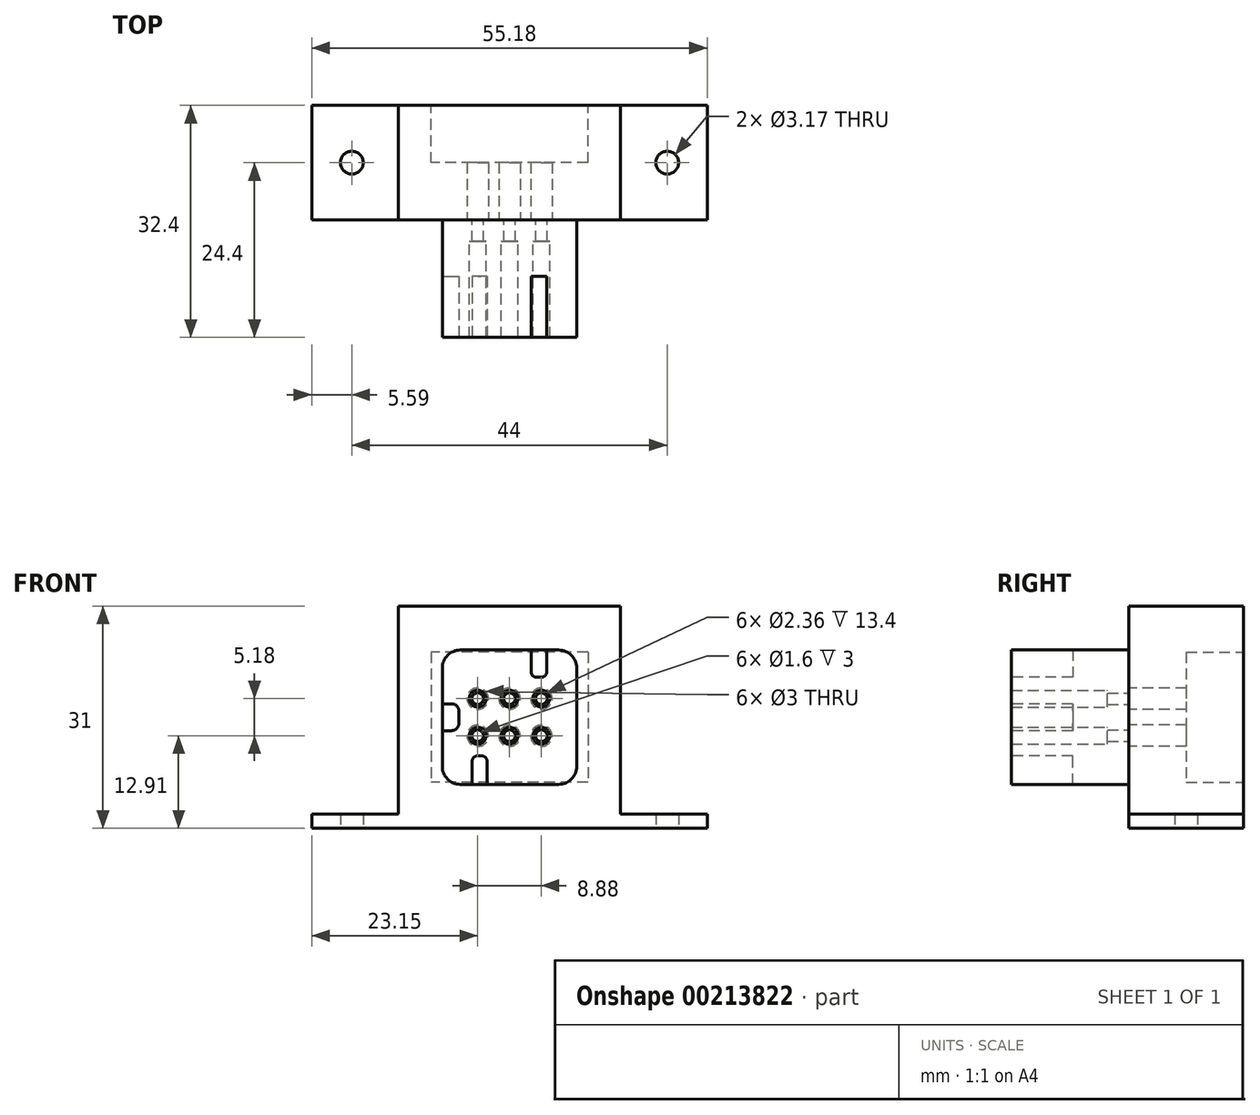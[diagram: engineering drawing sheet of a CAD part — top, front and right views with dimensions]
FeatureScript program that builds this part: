
annotation { "Feature Type Name" : "Feature", "Feature Type Description" : "" }
export const myFeature = defineFeature(function(context is Context, id is Id, definition is map)
    precondition{}
    {
        {
            var Q0;
            Q0=qCreatedBy(makeId("Front.planeOp"),FACE);
            var sketch = newSketch(context, id + "F0", { "sketchPlane" : qUnion([Q0])});
            skLineSegment(sketch, "E0.bottom", {"start": v(15.5, 15.5) * mm, "end": v(-15.5, 15.5) * mm});
            skLineSegment(sketch, "E0.top", {"start": v(15.5, -15.5) * mm, "end": v(-15.5, -15.5) * mm});
            skLineSegment(sketch, "E0.left", {"start": v(15.5, 15.5) * mm, "end": v(15.5, -15.5) * mm});
            skLineSegment(sketch, "E0.right", {"start": v(-15.5, 15.5) * mm, "end": v(-15.5, -15.5) * mm});
            skPoint(sketch, "E0.middle", {"position": v(0, 0) * mm});
            skCircle(sketch, "E1.0", {"center": v(-4.44, 2.6) * mm, "radius": 0.8 * mm, "construction": true});
            skCircle(sketch, "E2", {"center": v(-4.44, 2.6) * mm, "radius": 1.5 * mm});
            skCircle(sketch, "E3.1.0.0", {"center": v(0, 2.6) * mm, "radius": 1.5 * mm});
            skCircle(sketch, "E3.2.0.0", {"center": v(4.44, 2.6) * mm, "radius": 1.5 * mm});
            skLineSegment(sketch, "E3.direction1", {"start": v(-4.44, 2.6) * mm, "end": v(0, 2.6) * mm, "construction": true});
            skLineSegment(sketch, "E4", {"start": v(-15.5, 0) * mm, "end": v(15.5, 0) * mm, "construction": true});
            skCircle(sketch, "E5.MirrorC", {"center": v(-4.44, -2.6) * mm, "radius": 1.5 * mm});
            skCircle(sketch, "E6.MirrorC", {"center": v(0, -2.6) * mm, "radius": 1.5 * mm});
            skCircle(sketch, "E7.MirrorC", {"center": v(4.44, -2.6) * mm, "radius": 1.5 * mm});
            skLineSegment(sketch, "E8", {"start": v(0, 2.6) * mm, "end": v(0, -2.6) * mm, "construction": true});
            skSolve(sketch);
        }
        {
            var Q0;
            Q0 = qSketchRegion(id + "F0", true);
            extrude(context, id + "F1", {"entities" : qUnion([Q0]), "oppositeDirection" : true, "depth" : 16 * mm});
        }
        {
            var Q0;
            Q0=makeQuery(id+"F1.opExtrude","CAP_FACE",FACE,{"disambiguationData":[OSD([sQuery(id+"F0.wireOp",EDGE,"E0.bottom"),sQuery(id+"F0.wireOp",EDGE,"E0.top"),sQuery(id+"F0.wireOp",EDGE,"E0.left"),sQuery(id+"F0.wireOp",EDGE,"E0.right")])],"isStart":true});
            var sketch = newSketch(context, id + "F2", { "sketchPlane" : qUnion([Q0])});
            skLineSegment(sketch, "E9.bottom", {"start": v(6.87, 9.37) * mm, "end": v(-6.87, 9.37) * mm});
            skLineSegment(sketch, "E9.top", {"start": v(6.87, -9.37) * mm, "end": v(-6.87, -9.37) * mm});
            skLineSegment(sketch, "E9.left", {"start": v(9.37, 6.87) * mm, "end": v(9.37, -6.87) * mm});
            skLineSegment(sketch, "E9.right", {"start": v(-9.37, 6.87) * mm, "end": v(-9.37, -6.87) * mm});
            skPoint(sketch, "E9.middle", {"position": v(0, 0) * mm});
            skPoint(sketch, "E10.visualSharp", {"position": v(-9.37, 9.37) * mm});
            skArc(sketch, "E10.filletArc", {"start": v(-6.87, 9.37) * mm, "mid": v(-8.64, 8.64) * mm, "end": v(-9.37, 6.87) * mm});
            skPoint(sketch, "E11.visualSharp", {"position": v(9.37, 9.37) * mm});
            skArc(sketch, "E11.filletArc", {"start": v(9.37, 6.87) * mm, "mid": v(8.64, 8.64) * mm, "end": v(6.87, 9.37) * mm});
            skPoint(sketch, "E12.visualSharp", {"position": v(9.37, -9.37) * mm});
            skArc(sketch, "E12.filletArc", {"start": v(6.87, -9.37) * mm, "mid": v(8.64, -8.64) * mm, "end": v(9.37, -6.87) * mm});
            skPoint(sketch, "E13.visualSharp", {"position": v(-9.37, -9.37) * mm});
            skArc(sketch, "E13.filletArc", {"start": v(-9.37, -6.87) * mm, "mid": v(-8.64, -8.64) * mm, "end": v(-6.87, -9.37) * mm});
            skCircle(sketch, "E14", {"center": v(-4.44, 2.6) * mm, "radius": 1.18 * mm});
            skLineSegment(sketch, "E15", {"start": v(-9.37, 0) * mm, "end": v(9.37, 0) * mm, "construction": true});
            skCircle(sketch, "E16.1.0.0", {"center": v(0, 2.6) * mm, "radius": 1.18 * mm});
            skCircle(sketch, "E16.2.0.0", {"center": v(4.44, 2.6) * mm, "radius": 1.18 * mm});
            skLineSegment(sketch, "E16.direction1", {"start": v(-4.44, 2.6) * mm, "end": v(0, 2.6) * mm, "construction": true});
            skCircle(sketch, "E17.MirrorC", {"center": v(-4.44, -2.6) * mm, "radius": 1.18 * mm});
            skCircle(sketch, "E18.MirrorC", {"center": v(0, -2.6) * mm, "radius": 1.18 * mm});
            skCircle(sketch, "E19.MirrorC", {"center": v(4.44, -2.6) * mm, "radius": 1.18 * mm});
            skLineSegment(sketch, "E20.MirrorCS", {"start": v(-4.44, -2.6) * mm, "end": v(0, -2.6) * mm, "construction": true});
            skSolve(sketch);
        }
        {
            var Q0;
            Q0 = qSketchRegion(id + "F2", true);
            extrude(context, id + "F3", {"entities" : qUnion([Q0]), "depth" : 16.4 * mm});
        }
        {
            var Q0;
            Q0=makeQuery(id+"F3.opExtrude","CAP_FACE",FACE,{"disambiguationData":[OSD([sQuery(id+"F2.wireOp",EDGE,"E9.bottom"),sQuery(id+"F2.wireOp",EDGE,"E9.top"),sQuery(id+"F2.wireOp",EDGE,"E9.left"),sQuery(id+"F2.wireOp",EDGE,"E9.right"),sQuery(id+"F2.wireOp",EDGE,"E10.filletArc"),sQuery(id+"F2.wireOp",EDGE,"E11.filletArc"),sQuery(id+"F2.wireOp",EDGE,"E12.filletArc"),sQuery(id+"F2.wireOp",EDGE,"E13.filletArc"),sQuery(id+"F2.wireOp",EDGE,"E14"),sQuery(id+"F2.wireOp",EDGE,"E16.1.0.0"),sQuery(id+"F2.wireOp",EDGE,"E16.2.0.0"),sQuery(id+"F2.wireOp",EDGE,"E17.MirrorC"),sQuery(id+"F2.wireOp",EDGE,"E18.MirrorC"),sQuery(id+"F2.wireOp",EDGE,"E19.MirrorC")])],"isStart":false});
            var sketch = newSketch(context, id + "F4", { "sketchPlane" : qUnion([Q0])});
            skLineSegment(sketch, "E21.bottom", {"start": v(3, 9.37) * mm, "end": v(5.2, 9.37) * mm});
            skLineSegment(sketch, "E21.top", {"start": v(3.8, 5.57) * mm, "end": v(4.4, 5.57) * mm});
            skLineSegment(sketch, "E21.left", {"start": v(3, 9.37) * mm, "end": v(3, 6.37) * mm});
            skLineSegment(sketch, "E21.right", {"start": v(5.2, 9.37) * mm, "end": v(5.2, 6.37) * mm});
            skLineSegment(sketch, "E22.bottom", {"start": v(-5.22, -9.37) * mm, "end": v(-3.13, -9.37) * mm});
            skLineSegment(sketch, "E22.top", {"start": v(-4.42, -5.37) * mm, "end": v(-3.93, -5.37) * mm});
            skLineSegment(sketch, "E22.left", {"start": v(-5.22, -9.37) * mm, "end": v(-5.22, -6.17) * mm});
            skLineSegment(sketch, "E22.right", {"start": v(-3.13, -9.37) * mm, "end": v(-3.13, -6.17) * mm});
            skLineSegment(sketch, "E23.bottom", {"start": v(-9.37, 1.87) * mm, "end": v(-8.07, 1.87) * mm});
            skLineSegment(sketch, "E23.top", {"start": v(-9.37, -1.87) * mm, "end": v(-8.07, -1.87) * mm});
            skLineSegment(sketch, "E23.left", {"start": v(-9.37, 1.87) * mm, "end": v(-9.37, -1.87) * mm});
            skLineSegment(sketch, "E23.right", {"start": v(-7.07, 0.87) * mm, "end": v(-7.07, -0.87) * mm});
            skPoint(sketch, "E24.visualSharp", {"position": v(-7.07, 1.87) * mm});
            skArc(sketch, "E24.filletArc", {"start": v(-7.07, 0.87) * mm, "mid": v(-7.36, 1.58) * mm, "end": v(-8.07, 1.87) * mm});
            skPoint(sketch, "E25.visualSharp", {"position": v(-7.07, -1.87) * mm});
            skArc(sketch, "E25.filletArc", {"start": v(-8.07, -1.87) * mm, "mid": v(-7.36, -1.58) * mm, "end": v(-7.07, -0.87) * mm});
            skPoint(sketch, "E26.visualSharp", {"position": v(3, 5.57) * mm});
            skArc(sketch, "E26.filletArc", {"start": v(3, 6.37) * mm, "mid": v(3.24, 5.8) * mm, "end": v(3.8, 5.57) * mm});
            skPoint(sketch, "E27.visualSharp", {"position": v(5.2, 5.57) * mm});
            skArc(sketch, "E27.filletArc", {"start": v(4.4, 5.57) * mm, "mid": v(4.98, 5.8) * mm, "end": v(5.2, 6.37) * mm});
            skPoint(sketch, "E28.visualSharp", {"position": v(-5.22, -5.37) * mm});
            skArc(sketch, "E28.filletArc", {"start": v(-4.42, -5.37) * mm, "mid": v(-4.99, -5.6) * mm, "end": v(-5.22, -6.17) * mm});
            skPoint(sketch, "E29.visualSharp", {"position": v(-3.13, -5.37) * mm});
            skArc(sketch, "E29.filletArc", {"start": v(-3.13, -6.17) * mm, "mid": v(-3.36, -5.6) * mm, "end": v(-3.93, -5.37) * mm});
            skSolve(sketch);
        }
        {
            var Q0;
            Q0 = qSketchRegion(id + "F4", true);
            extrude(context, id + "F5", {"entities" : qUnion([Q0]), "operationType" : NewBodyOperationType.REMOVE, "oppositeDirection" : true, "depth" : 8.54 * mm});
        }
        {
            var Q0;
            Q0=makeQuery(id+"F2.imprint","IMPRINT",FACE,{"disambiguationData":[TD([[makeQuery(id+"F2.imprint","IMPRINT",EDGE,{"derivedFrom":sQuery(id+"F2.wireOp",EDGE,"E9.bottom")}),-1.0]])]});
            var sketch = newSketch(context, id + "F6", { "sketchPlane" : qUnion([Q0])});
            skCircle(sketch, "E30", {"center": v(-4.44, 2.6) * mm, "radius": 0.8 * mm});
            skCircle(sketch, "E31.1.0.0", {"center": v(0, 2.6) * mm, "radius": 0.8 * mm});
            skCircle(sketch, "E31.2.0.0", {"center": v(4.44, 2.6) * mm, "radius": 0.8 * mm});
            skLineSegment(sketch, "E31.direction1", {"start": v(-4.44, 2.6) * mm, "end": v(0, 2.6) * mm, "construction": true});
            skLineSegment(sketch, "E32.0", {"start": v(-9.37, 0) * mm, "end": v(9.37, 0) * mm, "construction": true});
            skCircle(sketch, "E33.MirrorC", {"center": v(-4.44, -2.6) * mm, "radius": 0.8 * mm});
            skCircle(sketch, "E34.MirrorC", {"center": v(0, -2.6) * mm, "radius": 0.8 * mm});
            skCircle(sketch, "E35.MirrorC", {"center": v(4.44, -2.6) * mm, "radius": 0.8 * mm});
            skCircle(sketch, "E36.0", {"center": v(4.44, 2.6) * mm, "radius": 1.18 * mm});
            skCircle(sketch, "E36.1", {"center": v(0, 2.6) * mm, "radius": 1.18 * mm});
            skCircle(sketch, "E36.2", {"center": v(-4.44, 2.6) * mm, "radius": 1.18 * mm});
            skCircle(sketch, "E36.3", {"center": v(-4.44, -2.6) * mm, "radius": 1.18 * mm});
            skCircle(sketch, "E36.4", {"center": v(0, -2.6) * mm, "radius": 1.18 * mm});
            skCircle(sketch, "E36.5", {"center": v(4.44, -2.6) * mm, "radius": 1.18 * mm});
            skSolve(sketch);
        }
        {
            var Q0;
            Q0 = qSketchRegion(id + "F6", true);
            extrude(context, id + "F7", {"entities" : qUnion([Q0]), "operationType" : NewBodyOperationType.ADD, "depth" : 3 * mm});
        }
        {
            var Q0;
            Q0=makeQuery(id+"F1.opExtrude","CAP_FACE",FACE,{"disambiguationData":[OSD([sQuery(id+"F0.wireOp",EDGE,"E0.bottom"),sQuery(id+"F0.wireOp",EDGE,"E0.top"),sQuery(id+"F0.wireOp",EDGE,"E0.left"),sQuery(id+"F0.wireOp",EDGE,"E0.right")])],"isStart":false});
            var sketch = newSketch(context, id + "F8", { "sketchPlane" : qUnion([Q0])});
            skLineSegment(sketch, "E37.bottom", {"start": v(-10.94, 9.1) * mm, "end": v(10.94, 9.1) * mm});
            skLineSegment(sketch, "E37.top", {"start": v(-10.94, -9.1) * mm, "end": v(10.94, -9.1) * mm});
            skLineSegment(sketch, "E37.left", {"start": v(-10.94, 9.1) * mm, "end": v(-10.94, -9.1) * mm});
            skLineSegment(sketch, "E37.right", {"start": v(10.94, 9.1) * mm, "end": v(10.94, -9.1) * mm});
            skSolve(sketch);
        }
        {
            var Q0;
            Q0 = qSketchRegion(id + "F8", true);
            extrude(context, id + "F9", {"entities" : qUnion([Q0]), "operationType" : NewBodyOperationType.REMOVE, "oppositeDirection" : true, "depth" : 8 * mm});
        }
        {
            var Q0;
            Q0=makeQuery(id+"F1.opExtrude","SWEPT_FACE",FACE,{"disambiguationData":[OSD([sQuery(id+"F0.wireOp",EDGE,"E0.top")])]});
            var sketch = newSketch(context, id + "F10", { "sketchPlane" : qUnion([Q0])});
            skLineSegment(sketch, "E38.bottom", {"start": v(-27.59, -16) * mm, "end": v(27.59, -16) * mm});
            skLineSegment(sketch, "E38.top", {"start": v(-27.59, 0) * mm, "end": v(-15.5, 0) * mm});
            skLineSegment(sketch, "E38.left", {"start": v(-27.59, -16) * mm, "end": v(-27.59, 0) * mm});
            skLineSegment(sketch, "E38.right", {"start": v(27.59, -16) * mm, "end": v(27.59, 0) * mm});
            skPoint(sketch, "E39.centerSnap0", {"position": v(-27.59, -8) * mm});
            skPoint(sketch, "E40.centerSnap0", {"position": v(27.59, -8) * mm});
            skLineSegment(sketch, "E41", {"start": v(-15.5, -16) * mm, "end": v(-15.5, 0) * mm});
            skLineSegment(sketch, "E42", {"start": v(15.5, 0) * mm, "end": v(15.5, -16) * mm});
            skLineSegment(sketch, "E43.trimOffspring", {"start": v(15.5, 0) * mm, "end": v(27.59, 0) * mm});
            skLineSegment(sketch, "E44", {"start": v(0, 0) * mm, "end": v(0, -16) * mm, "construction": true});
            skCircle(sketch, "E45", {"center": v(-22, -8) * mm, "radius": 1.59 * mm});
            skCircle(sketch, "E46.MirrorC", {"center": v(22, -8) * mm, "radius": 1.59 * mm});
            skSolve(sketch);
        }
        {
            var Q0;
            Q0 = qSketchRegion(id + "F10", true);
            extrude(context, id + "F11", {"entities" : qUnion([Q0]), "operationType" : NewBodyOperationType.ADD, "oppositeDirection" : true, "depth" : 2 * mm});
        }
    });
